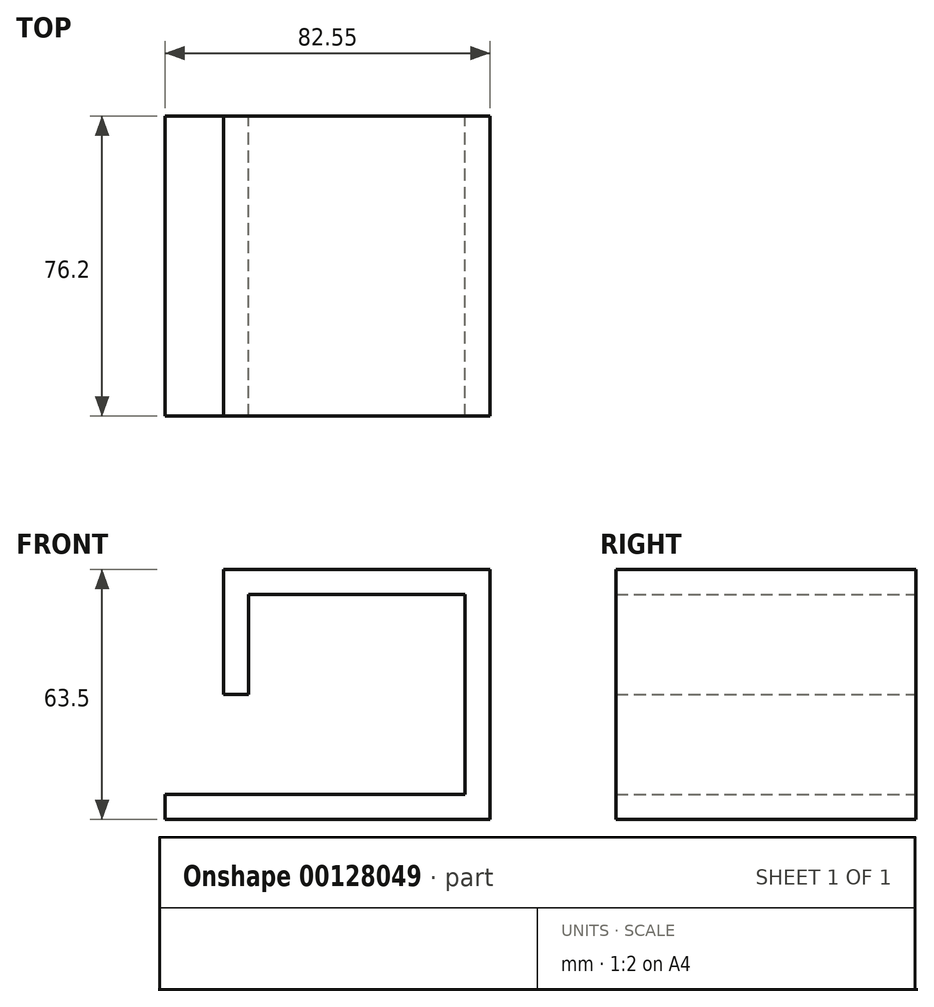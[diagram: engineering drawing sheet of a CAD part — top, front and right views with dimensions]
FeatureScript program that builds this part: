
annotation { "Feature Type Name" : "Feature", "Feature Type Description" : "" }
export const myFeature = defineFeature(function(context is Context, id is Id, definition is map)
    precondition{}
    {
        {
            var Q0;
            Q0=qCreatedBy(makeId("Front.planeOp"),FACE);
            var sketch = newSketch(context, id + "F0", { "sketchPlane" : qUnion([Q0])});
            skLineSegment(sketch, "E0", {"start": v(-46.67, -25.4) * mm, "end": v(29.53, -25.4) * mm});
            skLineSegment(sketch, "E1", {"start": v(29.53, -25.4) * mm, "end": v(29.53, 25.4) * mm});
            skLineSegment(sketch, "E2", {"start": v(29.53, 25.4) * mm, "end": v(-25.4, 25.4) * mm});
            skLineSegment(sketch, "E3", {"start": v(-25.4, 25.4) * mm, "end": v(-25.4, 0) * mm});
            skLineSegment(sketch, "E4.bottom", {"start": v(-50.8, 50.8) * mm, "end": v(50.8, 50.8) * mm});
            skLineSegment(sketch, "E4.top", {"start": v(-50.8, -50.8) * mm, "end": v(50.8, -50.8) * mm});
            skLineSegment(sketch, "E4.left", {"start": v(-50.8, 50.8) * mm, "end": v(-50.8, -50.8) * mm});
            skLineSegment(sketch, "E4.right", {"start": v(50.8, 50.8) * mm, "end": v(50.8, -50.8) * mm});
            skPoint(sketch, "E4.middle", {"position": v(0, 0) * mm});
            skLineSegment(sketch, "E5.0", {"start": v(-31.75, 31.75) * mm, "end": v(-31.75, 0) * mm});
            skLineSegment(sketch, "E5.1", {"start": v(35.88, 31.75) * mm, "end": v(-31.75, 31.75) * mm});
            skLineSegment(sketch, "E5.2", {"start": v(35.88, -31.75) * mm, "end": v(35.88, 31.75) * mm});
            skLineSegment(sketch, "E5.3", {"start": v(-46.67, -31.75) * mm, "end": v(35.88, -31.75) * mm});
            skLineSegment(sketch, "E6", {"start": v(-46.67, -31.75) * mm, "end": v(-46.67, -25.4) * mm});
            skLineSegment(sketch, "E7", {"start": v(-31.75, 0) * mm, "end": v(-25.4, 0) * mm});
            skLineSegment(sketch, "E8", {"start": v(-70.54, 87.47) * mm, "end": v(-70.54, 87.47) * mm});
            skSolve(sketch);
        }
        {
            var Q0;
            Q0=makeQuery(id+"F0.imprint","IMPRINT",FACE,{"disambiguationData":[TD([[makeQuery(id+"F0.imprint","IMPRINT",EDGE,{"derivedFrom":sQuery(id+"F0.wireOp",EDGE,"E0")}),-1.0]])]});
            var Q1;
            Q1=sQuery(id+"F0.wireOp",EDGE,"E4.left");
            var Q2;
            Q2=sQuery(id+"F0.wireOp",EDGE,"E4.bottom");
            var Q3;
            Q3=sQuery(id+"F0.wireOp",EDGE,"E4.right");
            var Q4;
            Q4=sQuery(id+"F0.wireOp",EDGE,"E4.top");
            extrude(context, id + "F1", {"entities" : qUnion([Q0]), "surfaceEntities" : qUnion([Q1, Q2, Q3, Q4]), "endBound" : BoundingType.SYMMETRIC, "depth" : 76.2 * mm});
        }
    });
